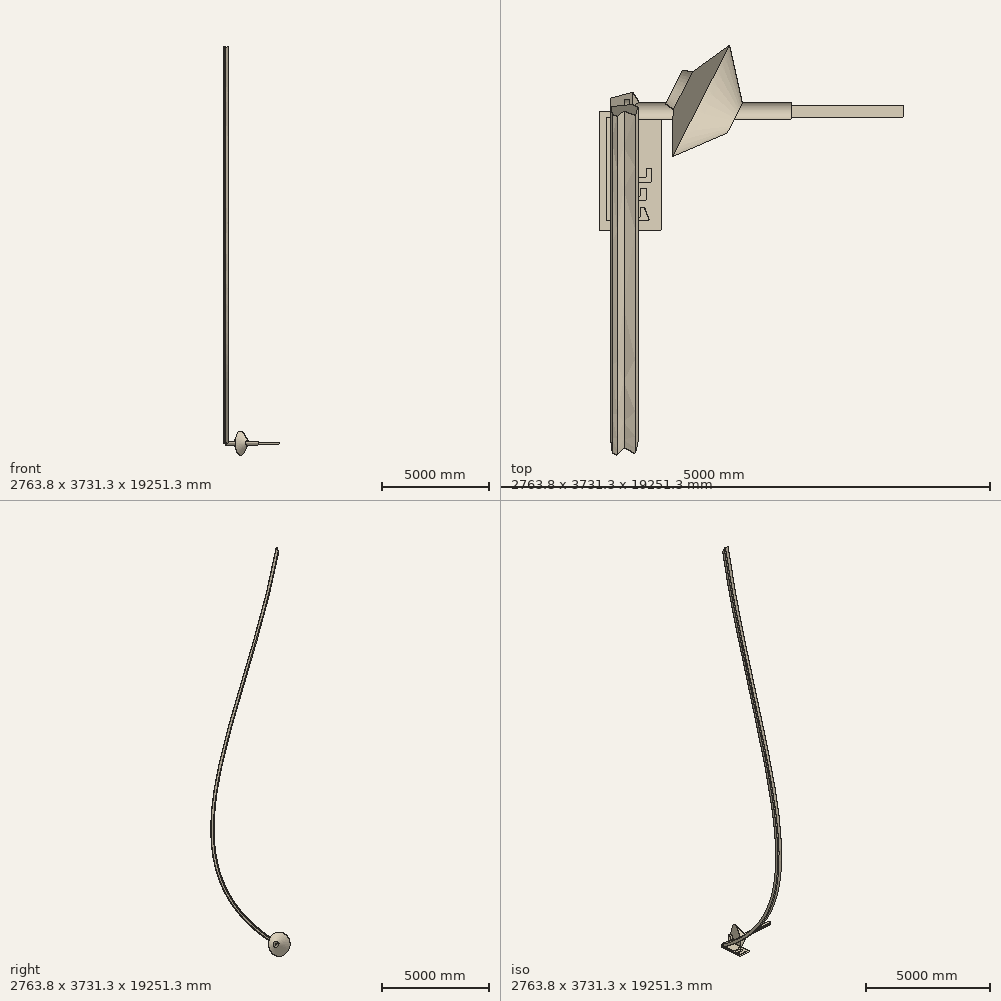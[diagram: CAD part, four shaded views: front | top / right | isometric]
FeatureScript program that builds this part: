
annotation { "Feature Type Name" : "Feature", "Feature Type Description" : "" }
export const myFeature = defineFeature(function(context is Context, id is Id, definition is map)
    precondition{}
    {
        {
            var Q0;
            Q0=qCreatedBy(makeId("Top.planeOp"),FACE);
            var sketch = newSketch(context, id + "F0", { "sketchPlane" : qUnion([Q0])});
            skLineSegment(sketch, "E0", {"start": v(-120.09, 119.37) * mm, "end": v(104.44, -103.82) * mm});
            skLineSegment(sketch, "E1", {"start": v(-60.3, -131.92) * mm, "end": v(78.89, 172.56) * mm});
            skLineSegment(sketch, "E2", {"start": v(-106.9, -85.12) * mm, "end": v(127.2, 101.28) * mm});
            skLineSegment(sketch, "E3", {"start": v(374.94, 62.54) * mm, "end": v(938.99, -198.65) * mm});
            skLineSegment(sketch, "E4", {"start": v(441.44, -413.88) * mm, "end": v(441.44, 0) * mm});
            skLineSegment(sketch, "E5", {"start": v(-1752.16, -22225.03) * mm, "end": v(144.42, -12218.76) * mm});
            skLineSegment(sketch, "E6", {"start": v(144.42, -12218.76) * mm, "end": v(-2779.6, -37150.94) * mm});
            skLineSegment(sketch, "E7", {"start": v(-2779.6, -37150.94) * mm, "end": v(-393.6, -21114.09) * mm});
            skLineSegment(sketch, "E8", {"start": v(104.44, -103.82) * mm, "end": v(127.2, 101.28) * mm});
            skLineSegment(sketch, "E9", {"start": v(127.2, 101.28) * mm, "end": v(78.89, 172.56) * mm});
            skLineSegment(sketch, "E10", {"start": v(-120.09, 119.37) * mm, "end": v(-106.9, -85.12) * mm});
            skLineSegment(sketch, "E11", {"start": v(-60.3, -131.92) * mm, "end": v(-60.3, -131.92) * mm});
            skLineSegment(sketch, "E12", {"start": v(-120.09, 119.37) * mm, "end": v(78.89, 172.56) * mm});
            skLineSegment(sketch, "E13", {"start": v(-106.9, -85.12) * mm, "end": v(-60.3, -131.92) * mm});
            skLineSegment(sketch, "E14", {"start": v(-57.87, -126.6) * mm, "end": v(104.44, -103.82) * mm});
            skLineSegment(sketch, "E15", {"start": v(441.44, 0) * mm, "end": v(374.94, 62.54) * mm});
            skLineSegment(sketch, "E16", {"start": v(441.44, -413.88) * mm, "end": v(938.99, -198.65) * mm});
            skLineSegment(sketch, "E17", {"start": v(322.4, 286) * mm, "end": v(1222.34, -174.43) * mm, "construction": true});
            skSolve(sketch);
        }
        {
            var Q0;
            Q0=makeQuery(id+"F0.imprint","IMPRINT",FACE,{"disambiguationData":[TD([[makeQuery(id+"F0.imprint","IMPRINT",EDGE,{"derivedFrom":sQuery(id+"F0.wireOp",EDGE,"E3")}),-1.0]])]});
            var Q1;
            Q1=sQuery(id+"F0.wireOp",EDGE,"E17");
            revolve(context, id + "F1", {"entities" : qUnion([Q0]), "axis" : qUnion([Q1]), "revolveType" : RevolveType.FULL});
        }
        {
            var Q0;
            Q0=qCreatedBy(makeId("Right.planeOp"),FACE);
            var sketch = newSketch(context, id + "F2", { "sketchPlane" : qUnion([Q0])});
            skFitSpline(sketch, "E18", {"points": [v(0, 0) * mm, v(0, 18559.35) * mm], "startDerivative": vector(-18198.9, 11176.24) * mm, "endDerivative": vector(4513.45, 24290.18) * mm});
            skSolve(sketch);
        }
        {
            var Q0;
            {var subQ0=sQuery(id+"F0.wireOp",EDGE,"E12");Q0=makeQuery(id+"F0.imprint","IMPRINT",FACE,{"disambiguationData":[TD([[makeQuery(id+"F0.imprint","IMPRINT",EDGE,{"derivedFrom":subQ0}),-1.0]])]});}
            var Q1;
            {var subQ0=sQuery(id+"F0.wireOp",EDGE,"E9");Q1=makeQuery(id+"F0.imprint","IMPRINT",FACE,{"disambiguationData":[TD([[makeQuery(id+"F0.imprint","IMPRINT",EDGE,{"derivedFrom":subQ0}),1.0]])]});}
            var Q2;
            {var subQ0=sQuery(id+"F0.wireOp",EDGE,"E8");Q2=makeQuery(id+"F0.imprint","IMPRINT",FACE,{"disambiguationData":[TD([[makeQuery(id+"F0.imprint","IMPRINT",EDGE,{"derivedFrom":subQ0}),1.0]])]});}
            var Q3;
            {var subQ0=sQuery(id+"F0.wireOp",EDGE,"E13");Q3=makeQuery(id+"F0.imprint","IMPRINT",FACE,{"disambiguationData":[TD([[makeQuery(id+"F0.imprint","IMPRINT",EDGE,{"derivedFrom":subQ0}),1.0]])]});}
            var Q4;
            {var subQ0=sQuery(id+"F0.wireOp",EDGE,"E10");Q4=makeQuery(id+"F0.imprint","IMPRINT",FACE,{"disambiguationData":[TD([[makeQuery(id+"F0.imprint","IMPRINT",EDGE,{"derivedFrom":subQ0}),1.0]])]});}
            var Q5;
            Q5=sQuery(id+"F2.wireOp",EDGE,"E18");
            sweep(context, id + "F3", {"profiles" : qUnion([Q0, Q1, Q2, Q3, Q4]), "path" : qUnion([Q5])});
        }
        {
            var Q0;
            Q0=qCreatedBy(makeId("Right.planeOp"),FACE);
            var sketch = newSketch(context, id + "F4", { "sketchPlane" : qUnion([Q0])});
            skLineSegment(sketch, "E19", {"start": v(-55.8, -46.7) * mm, "end": v(-55.8, -71.05) * mm});
            skLineSegment(sketch, "E20", {"start": v(-55.8, -71.05) * mm, "end": v(55.7, -71.39) * mm});
            skLineSegment(sketch, "E21", {"start": v(55.7, -71.39) * mm, "end": v(55.91, -46.16) * mm});
            skLineSegment(sketch, "E22", {"start": v(55.91, -46.16) * mm, "end": v(20.82, -45.86) * mm});
            skLineSegment(sketch, "E23", {"start": v(20.82, -45.86) * mm, "end": v(11.44, 30.4) * mm});
            skLineSegment(sketch, "E24", {"start": v(11.44, 30.4) * mm, "end": v(56.96, 36) * mm});
            skLineSegment(sketch, "E25", {"start": v(56.96, 36) * mm, "end": v(53.21, 54.83) * mm});
            skLineSegment(sketch, "E26", {"start": v(53.21, 54.83) * mm, "end": v(-51.92, 54.83) * mm});
            skLineSegment(sketch, "E27", {"start": v(-51.92, 54.83) * mm, "end": v(-51.92, 40.8) * mm});
            skLineSegment(sketch, "E28", {"start": v(-51.92, 40.8) * mm, "end": v(-12.63, 31.15) * mm});
            skLineSegment(sketch, "E29", {"start": v(-12.63, 31.15) * mm, "end": v(-12.63, -30.71) * mm});
            skLineSegment(sketch, "E30", {"start": v(-12.63, -30.71) * mm, "end": v(-55.8, -46.7) * mm});
            skSolve(sketch);
        }
        {
            var Q0;
            Q0 = qSketchRegion(id + "F4", true);
            extrude(context, id + "F5", {"entities" : qUnion([Q0]), "depth" : 2540 * mm});
        }
        {
            var Q0;
            Q0=qCreatedBy(makeId("Right.planeOp"),FACE);
            var sketch = newSketch(context, id + "F6", { "sketchPlane" : qUnion([Q0])});
            skCircle(sketch, "E31", {"center": v(0, 0) * mm, "radius": 110.6 * mm});
            skCircle(sketch, "E32", {"center": v(0, 0) * mm, "radius": 76.68 * mm});
            skCircle(sketch, "E33", {"center": v(70.91, -65.11) * mm, "radius": 11.09 * mm});
            skCircle(sketch, "E34.1.0", {"center": v(96.18, -4.3) * mm, "radius": 11.09 * mm});
            skCircle(sketch, "E34.2.0", {"center": v(76.44, 58.53) * mm, "radius": 11.09 * mm});
            skCircle(sketch, "E34.3.0", {"center": v(20.93, 93.97) * mm, "radius": 11.09 * mm});
            skCircle(sketch, "E34.4.0", {"center": v(-44.37, 85.44) * mm, "radius": 11.09 * mm});
            skCircle(sketch, "E34.5.0", {"center": v(-88.9, 36.93) * mm, "radius": 11.09 * mm});
            skCircle(sketch, "E34.6.0", {"center": v(-91.85, -28.86) * mm, "radius": 11.09 * mm});
            skCircle(sketch, "E34.7.0", {"center": v(-51.81, -81.14) * mm, "radius": 11.09 * mm});
            skCircle(sketch, "E34.8.0", {"center": v(12.47, -95.46) * mm, "radius": 11.09 * mm});
            skCircle(sketch, "E35", {"center": v(0, 0) * mm, "radius": 70.07 * mm});
            skSolve(sketch);
        }
        {
            var Q0;
            Q0=makeQuery(id+"F6.imprint","IMPRINT",FACE,{"disambiguationData":[TD([[makeQuery(id+"F6.imprint","IMPRINT",EDGE,{"derivedFrom":sQuery(id+"F6.wireOp",EDGE,"E32")}),1.0]])]});
            extrude(context, id + "F7", {"entities" : qUnion([Q0]), "depth" : 1524 * mm});
        }
        {
            var Q0;
            Q0 = qSketchRegion(id + "FBbvTtz5Uz4uK3I_4", true);
            var Q1;
            Q1=makeQuery(id+"F6.imprint","IMPRINT",FACE,{"disambiguationData":[TD([[makeQuery(id+"F6.imprint","IMPRINT",EDGE,{"derivedFrom":sQuery(id+"F6.wireOp",EDGE,"E31")}),1.0]])]});
            extrude(context, id + "F8", {"entities" : qUnion([Q0, Q1]), "depth" : 50.8 * mm});
        }
        {
            var Q0;
            Q0=qCreatedBy(makeId("Top.planeOp"),FACE);
            var sketch = newSketch(context, id + "F9", { "sketchPlane" : qUnion([Q0])});
            skLineSegment(sketch, "E36.bottom", {"start": v(-223.75, 0) * mm, "end": v(343.75, 0) * mm});
            skLineSegment(sketch, "E36.top", {"start": v(-223.75, -1087.04) * mm, "end": v(343.75, -1087.04) * mm});
            skLineSegment(sketch, "E36.left", {"start": v(-223.75, 0) * mm, "end": v(-223.75, -1087.04) * mm});
            skLineSegment(sketch, "E36.right", {"start": v(343.75, 0) * mm, "end": v(343.75, -1087.04) * mm});
            skPoint(sketch, "E36.middle", {"position": v(60, -543.52) * mm});
            skSolve(sketch);
        }
        {
            var Q0;
            Q0 = qSketchRegion(id + "F9", true);
            extrude(context, id + "F10", {"entities" : qUnion([Q0]), "depth" : 0.76 * mm});
        }
        {
            var Q0;
            Q0=makeQuery(id+"F10.opExtrude","CAP_FACE",FACE,{"disambiguationData":[OSD([sQuery(id+"F9.wireOp",EDGE,"E36.bottom"),sQuery(id+"F9.wireOp",EDGE,"E36.top"),sQuery(id+"F9.wireOp",EDGE,"E36.left"),sQuery(id+"F9.wireOp",EDGE,"E36.right")])],"isStart":false});
            var sketch = newSketch(context, id + "F11", { "sketchPlane" : qUnion([Q0])});
            skLineSegment(sketch, "E37", {"start": v(-156.7, -59.61) * mm, "end": v(-156.7, -997.01) * mm});
            skLineSegment(sketch, "E38", {"start": v(-156.7, -997.01) * mm, "end": v(233.31, -997.01) * mm});
            skLineSegment(sketch, "E39", {"start": v(233.31, -997.01) * mm, "end": v(186.35, -878.64) * mm});
            skLineSegment(sketch, "E40", {"start": v(186.35, -878.64) * mm, "end": v(145.32, -878.64) * mm});
            skLineSegment(sketch, "E41", {"start": v(145.32, -878.64) * mm, "end": v(145.32, -965.42) * mm});
            skLineSegment(sketch, "E42", {"start": v(145.32, -965.42) * mm, "end": v(-110.08, -965.42) * mm});
            skLineSegment(sketch, "E43", {"start": v(-110.08, -965.42) * mm, "end": v(-110.08, -813.55) * mm});
            skLineSegment(sketch, "E44", {"start": v(-110.08, -813.55) * mm, "end": v(201.44, -813.55) * mm});
            skLineSegment(sketch, "E45", {"start": v(201.44, -813.55) * mm, "end": v(201.44, -699.65) * mm});
            skLineSegment(sketch, "E46", {"start": v(201.44, -699.65) * mm, "end": v(146.68, -699.65) * mm});
            skLineSegment(sketch, "E47", {"start": v(146.68, -699.65) * mm, "end": v(146.68, -773.03) * mm});
            skLineSegment(sketch, "E48", {"start": v(146.68, -773.03) * mm, "end": v(-106.39, -773.03) * mm});
            skLineSegment(sketch, "E49", {"start": v(-106.39, -773.03) * mm, "end": v(-106.39, -645.73) * mm});
            skLineSegment(sketch, "E50", {"start": v(-106.39, -645.73) * mm, "end": v(251.66, -645.73) * mm});
            skLineSegment(sketch, "E51", {"start": v(251.66, -645.73) * mm, "end": v(251.66, -520.97) * mm});
            skLineSegment(sketch, "E52", {"start": v(251.66, -520.97) * mm, "end": v(206.77, -520.97) * mm});
            skLineSegment(sketch, "E53", {"start": v(206.77, -520.97) * mm, "end": v(206.77, -605.84) * mm});
            skLineSegment(sketch, "E54", {"start": v(206.77, -605.84) * mm, "end": v(-106.29, -605.84) * mm});
            skLineSegment(sketch, "E55", {"start": v(-106.29, -605.84) * mm, "end": v(-106.29, -59.61) * mm});
            skLineSegment(sketch, "E56", {"start": v(-106.29, -59.61) * mm, "end": v(-156.7, -59.61) * mm});
            skSolve(sketch);
        }
        {
            var Q0;
            Q0 = qSketchRegion(id + "F11", true);
            extrude(context, id + "F12", {"entities" : qUnion([Q0]), "depth" : 0.38 * mm});
        }
        {
            var Q0;
            Q0=makeQuery(id+"F12.opExtrude","CAP_EDGE",EDGE,{"disambiguationData":[OSD([sQuery(id+"F11.wireOp",EDGE,"E42")])],"isStart":false});
            var Q1;
            Q1=makeQuery(id+"F12.opExtrude","CAP_EDGE",EDGE,{"disambiguationData":[OSD([sQuery(id+"F11.wireOp",EDGE,"E38")])],"isStart":false});
            var Q2;
            Q2=makeQuery(id+"F12.opExtrude","CAP_EDGE",EDGE,{"disambiguationData":[OSD([sQuery(id+"F11.wireOp",EDGE,"E43")])],"isStart":false});
            var Q3;
            Q3=makeQuery(id+"F12.opExtrude","CAP_EDGE",EDGE,{"disambiguationData":[OSD([sQuery(id+"F11.wireOp",EDGE,"E39")])],"isStart":false});
            var Q4;
            Q4=makeQuery(id+"F12.opExtrude","CAP_EDGE",EDGE,{"disambiguationData":[OSD([sQuery(id+"F11.wireOp",EDGE,"E40")])],"isStart":false});
            var Q5;
            Q5=makeQuery(id+"F12.opExtrude","CAP_EDGE",EDGE,{"disambiguationData":[OSD([sQuery(id+"F11.wireOp",EDGE,"E41")])],"isStart":false});
            var Q6;
            Q6=makeQuery(id+"F12.opExtrude","CAP_EDGE",EDGE,{"disambiguationData":[OSD([sQuery(id+"F11.wireOp",EDGE,"E44")])],"isStart":false});
            var Q7;
            Q7=makeQuery(id+"F12.opExtrude","CAP_EDGE",EDGE,{"disambiguationData":[OSD([sQuery(id+"F11.wireOp",EDGE,"E45")])],"isStart":false});
            var Q8;
            Q8=makeQuery(id+"F12.opExtrude","CAP_EDGE",EDGE,{"disambiguationData":[OSD([sQuery(id+"F11.wireOp",EDGE,"E46")])],"isStart":false});
            var Q9;
            Q9=makeQuery(id+"F12.opExtrude","CAP_EDGE",EDGE,{"disambiguationData":[OSD([sQuery(id+"F11.wireOp",EDGE,"E47")])],"isStart":false});
            var Q10;
            Q10=makeQuery(id+"F12.opExtrude","CAP_EDGE",EDGE,{"disambiguationData":[OSD([sQuery(id+"F11.wireOp",EDGE,"E48")])],"isStart":false});
            var Q11;
            Q11=makeQuery(id+"F12.opExtrude","CAP_FACE",FACE,{"disambiguationData":[OSD([sQuery(id+"F11.wireOp",EDGE,"E37"),sQuery(id+"F11.wireOp",EDGE,"E38"),sQuery(id+"F11.wireOp",EDGE,"E39"),sQuery(id+"F11.wireOp",EDGE,"E40"),sQuery(id+"F11.wireOp",EDGE,"E41"),sQuery(id+"F11.wireOp",EDGE,"E42"),sQuery(id+"F11.wireOp",EDGE,"E43"),sQuery(id+"F11.wireOp",EDGE,"E44"),sQuery(id+"F11.wireOp",EDGE,"E45"),sQuery(id+"F11.wireOp",EDGE,"E46"),sQuery(id+"F11.wireOp",EDGE,"E47"),sQuery(id+"F11.wireOp",EDGE,"E48"),sQuery(id+"F11.wireOp",EDGE,"E49"),sQuery(id+"F11.wireOp",EDGE,"E50"),sQuery(id+"F11.wireOp",EDGE,"E51"),sQuery(id+"F11.wireOp",EDGE,"E52"),sQuery(id+"F11.wireOp",EDGE,"E53"),sQuery(id+"F11.wireOp",EDGE,"E54"),sQuery(id+"F11.wireOp",EDGE,"E55"),sQuery(id+"F11.wireOp",EDGE,"E56")])],"isStart":false});
            var Q12;
            Q12=makeQuery(id+"F12.opExtrude","CAP_EDGE",EDGE,{"disambiguationData":[OSD([sQuery(id+"F11.wireOp",EDGE,"E49")])],"isStart":false});
            var Q13;
            Q13=makeQuery(id+"F12.opExtrude","CAP_EDGE",EDGE,{"disambiguationData":[OSD([sQuery(id+"F11.wireOp",EDGE,"E50")])],"isStart":false});
            var Q14;
            Q14=makeQuery(id+"F12.opExtrude","CAP_EDGE",EDGE,{"disambiguationData":[OSD([sQuery(id+"F11.wireOp",EDGE,"E51")])],"isStart":false});
            var Q15;
            Q15=makeQuery(id+"F12.opExtrude","CAP_EDGE",EDGE,{"disambiguationData":[OSD([sQuery(id+"F11.wireOp",EDGE,"E52")])],"isStart":false});
            var Q16;
            Q16=makeQuery(id+"F12.opExtrude","CAP_EDGE",EDGE,{"disambiguationData":[OSD([sQuery(id+"F11.wireOp",EDGE,"E53")])],"isStart":false});
            var Q17;
            Q17=makeQuery(id+"F12.opExtrude","CAP_EDGE",EDGE,{"disambiguationData":[OSD([sQuery(id+"F11.wireOp",EDGE,"E54")])],"isStart":false});
            var Q18;
            Q18=makeQuery(id+"F12.opExtrude","CAP_EDGE",EDGE,{"disambiguationData":[OSD([sQuery(id+"F11.wireOp",EDGE,"E55")])],"isStart":false});
            var Q19;
            Q19=makeQuery(id+"F12.opExtrude","CAP_EDGE",EDGE,{"disambiguationData":[OSD([sQuery(id+"F11.wireOp",EDGE,"E56")])],"isStart":false});
            var Q20;
            Q20=makeQuery(id+"F12.opExtrude","CAP_EDGE",EDGE,{"disambiguationData":[OSD([sQuery(id+"F11.wireOp",EDGE,"E37")])],"isStart":false});
            fillet(context, id + "F13", {"entities" : qUnion([Q0, Q1, Q2, Q3, Q4, Q5, Q6, Q7, Q8, Q9, Q10, Q11, Q12, Q13, Q14, Q15, Q16, Q17, Q18, Q19, Q20]), "radius" : 0.1 * mm, "allowEdgeOverflow" : false});
        }
    });
